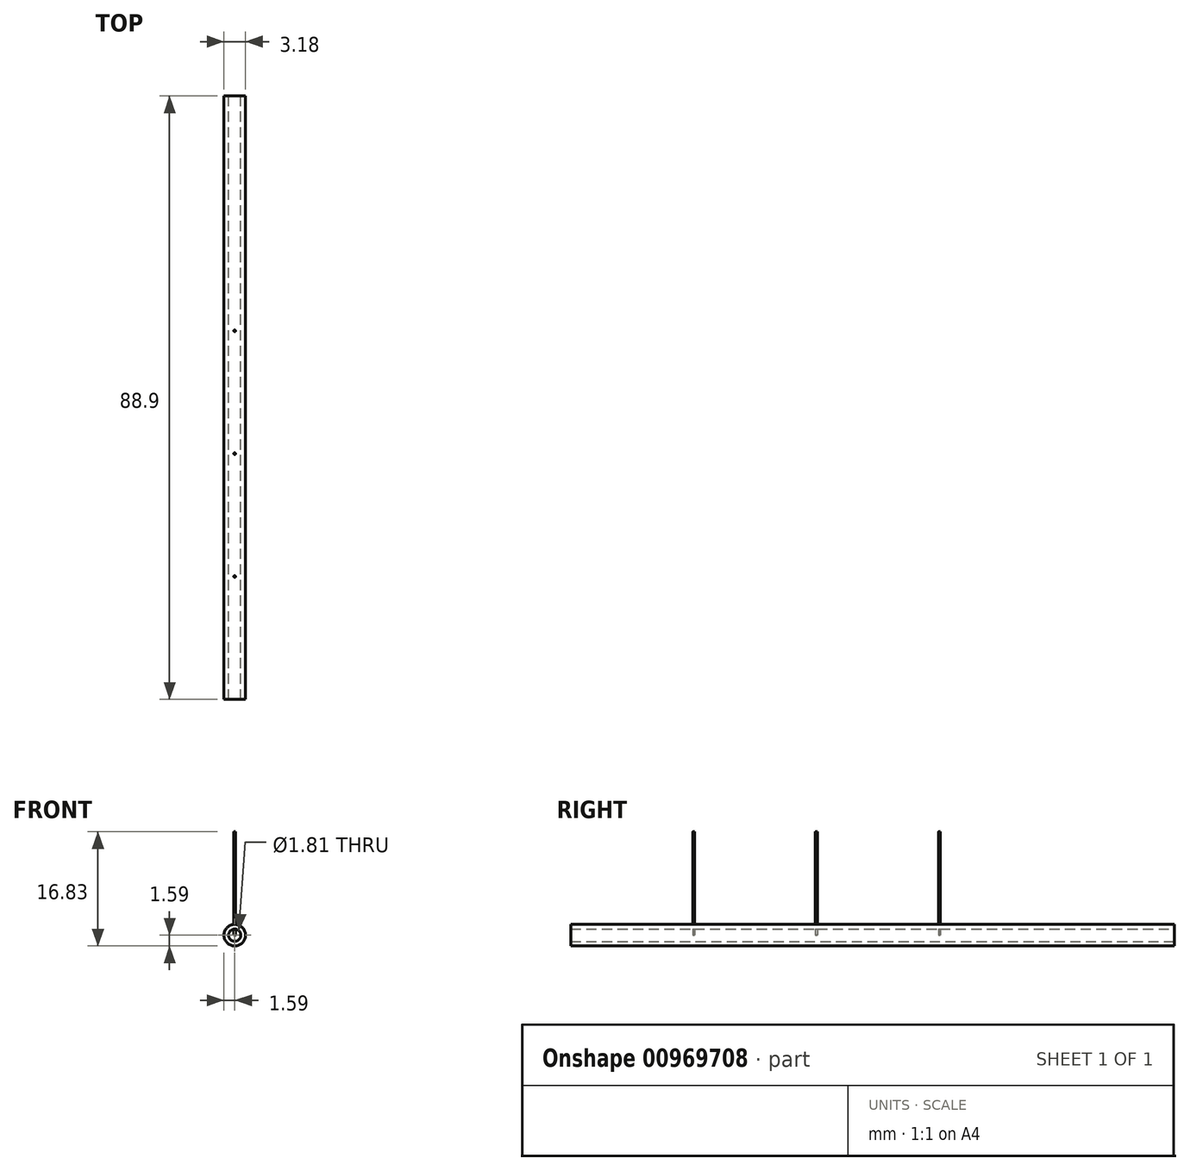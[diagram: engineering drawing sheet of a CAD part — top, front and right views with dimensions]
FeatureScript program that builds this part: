
annotation { "Feature Type Name" : "Feature", "Feature Type Description" : "" }
export const myFeature = defineFeature(function(context is Context, id is Id, definition is map)
    precondition{}
    {
        {
            var Q0;
            Q0=qCreatedBy(makeId("Front.planeOp"),FACE);
            var sketch = newSketch(context, id + "F0", { "sketchPlane" : qUnion([Q0])});
            skCircle(sketch, "E0", {"center": v(0, 0) * mm, "radius": 1.59 * mm});
            skCircle(sketch, "E1", {"center": v(0, 0) * mm, "radius": 0.9 * mm});
            skSolve(sketch);
        }
        {
            var Q0;
            Q0 = qSketchRegion(id + "F0", true);
            extrude(context, id + "F1", {"entities" : qUnion([Q0]), "depth" : 88.9 * mm, "offsetDistance" : 25.4 * mm});
        }
        {
            var Q0;
            Q0=qCreatedBy(makeId("Top.planeOp"),FACE);
            var sketch = newSketch(context, id + "F2", { "sketchPlane" : qUnion([Q0])});
            skCircle(sketch, "E2", {"center": v(0, -70.8) * mm, "radius": 0.13 * mm});
            skCircle(sketch, "E3", {"center": v(0, -34.6) * mm, "radius": 0.13 * mm});
            skCircle(sketch, "E4", {"center": v(0, -52.7) * mm, "radius": 0.13 * mm});
            skSolve(sketch);
        }
        {
            var Q0;
            Q0 = qSketchRegion(id + "F2", true);
            extrude(context, id + "F3", {"entities" : qUnion([Q0]), "operationType" : NewBodyOperationType.ADD, "depth" : 15.24 * mm, "offsetDistance" : 25.4 * mm});
        }
    });
